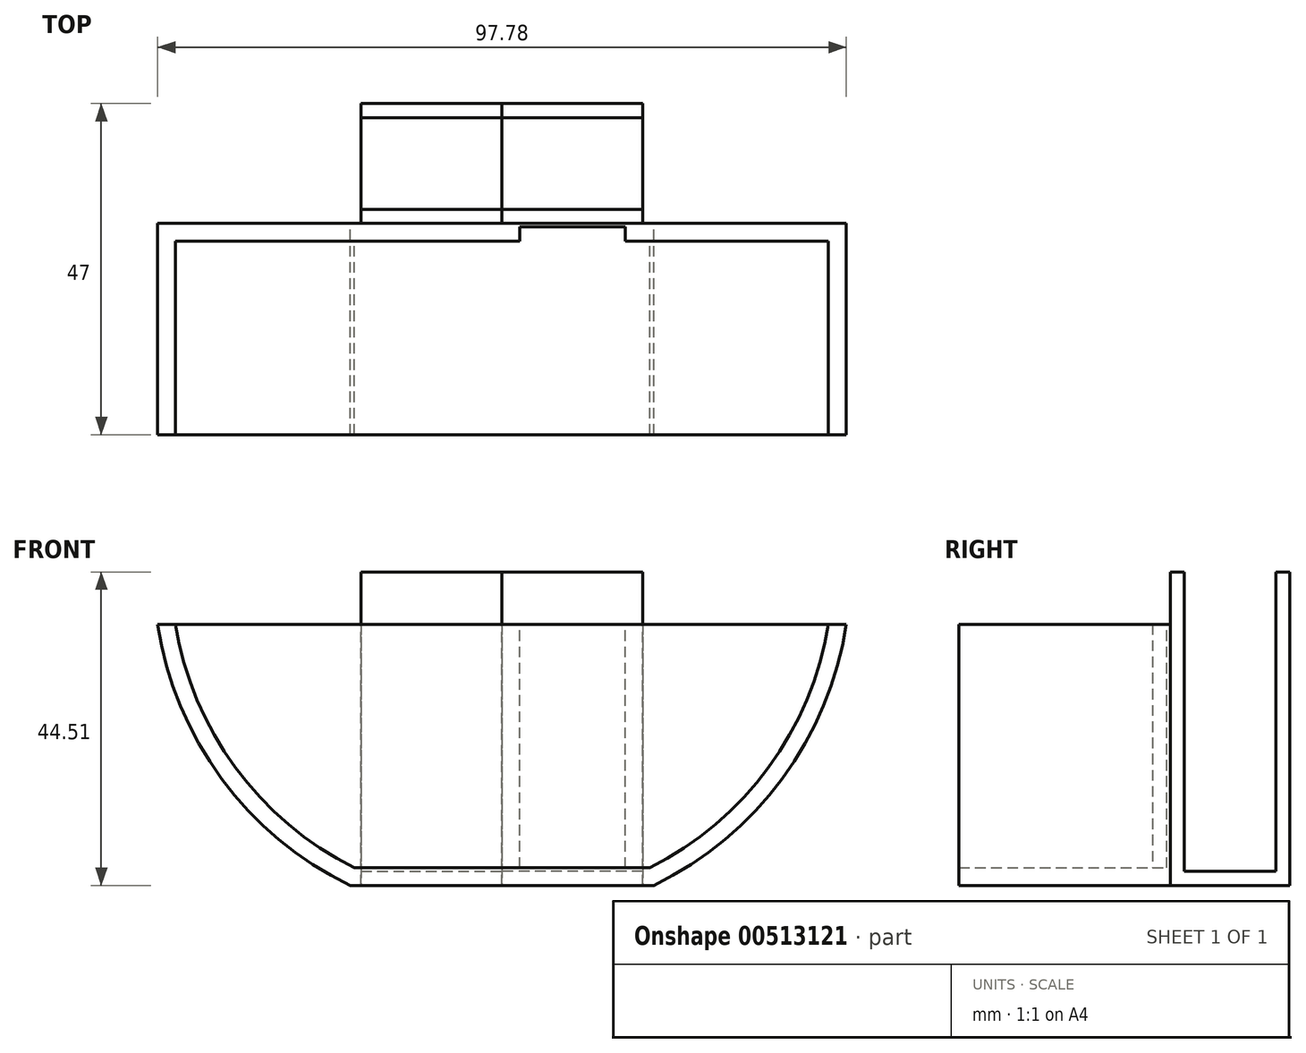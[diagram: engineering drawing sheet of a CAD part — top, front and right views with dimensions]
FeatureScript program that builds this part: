
annotation { "Feature Type Name" : "Feature", "Feature Type Description" : "" }
export const myFeature = defineFeature(function(context is Context, id is Id, definition is map)
    precondition{}
    {
        {
            var Q0;
            Q0=qCreatedBy(makeId("Front.planeOp"),FACE);
            var sketch = newSketch(context, id + "F0", { "sketchPlane" : qUnion([Q0])});
            skCircle(sketch, "E0", {"center": v(0, 0) * mm, "radius": 49.45 * mm});
            skLineSegment(sketch, "E1", {"start": v(-48.9, -7.42) * mm, "end": v(48.9, -7.42) * mm});
            skLineSegment(sketch, "E2", {"start": v(-21.56, -44.5) * mm, "end": v(21.56, -44.5) * mm});
            skSolve(sketch);
        }
        {
            var Q0;
            Q0=qCreatedBy(makeId("Right.planeOp"),FACE);
            var sketch = newSketch(context, id + "F1", { "sketchPlane" : qUnion([Q0])});
            skLineSegment(sketch, "E3", {"start": v(0, -44.5) * mm, "end": v(17, -44.5) * mm});
            skLineSegment(sketch, "E4", {"start": v(17, -44.5) * mm, "end": v(17, 0) * mm});
            skLineSegment(sketch, "E5", {"start": v(17, 0) * mm, "end": v(15, 0) * mm});
            skLineSegment(sketch, "E6", {"start": v(15, 0) * mm, "end": v(15, -42.5) * mm});
            skLineSegment(sketch, "E7", {"start": v(15, -42.5) * mm, "end": v(2, -42.5) * mm});
            skLineSegment(sketch, "E8", {"start": v(2, -42.5) * mm, "end": v(2, 0) * mm});
            skLineSegment(sketch, "E9", {"start": v(2, 0) * mm, "end": v(0, 0) * mm});
            skLineSegment(sketch, "E10", {"start": v(0, 0) * mm, "end": v(0, -44.5) * mm});
            skSolve(sketch);
        }
        {
            var Q0;
            Q0 = qSketchRegion(id + "F1", true);
            extrude(context, id + "F2", {"entities" : qUnion([Q0]), "depth" : 20 * mm});
        }
        {
            var Q0;
            {var subQ0=sQuery(id+"F0.wireOp",EDGE,"E1");Q0=makeQuery(id+"F0.imprint","IMPRINT",FACE,{"disambiguationData":[TD([[makeQuery(id+"F0.imprint","IMPRINT",EDGE,{"derivedFrom":subQ0}),-1.0]])]});}
            extrude(context, id + "F3", {"entities" : qUnion([Q0]), "operationType" : NewBodyOperationType.ADD, "depth" : 30 * mm});
        }
        {
            var Q0;
            Q0=makeQuery(id+"F2.opExtrude","SWEPT_BODY",BODY,{"disambiguationData":[OSD([sQuery(id+"F1.wireOp",EDGE,"E3"),sQuery(id+"F1.wireOp",EDGE,"E4"),sQuery(id+"F1.wireOp",EDGE,"E5"),sQuery(id+"F1.wireOp",EDGE,"E6"),sQuery(id+"F1.wireOp",EDGE,"E7"),sQuery(id+"F1.wireOp",EDGE,"E8"),sQuery(id+"F1.wireOp",EDGE,"E9"),sQuery(id+"F1.wireOp",EDGE,"E10")])]});
            var Q1;
            Q1=qCreatedBy(makeId("Right.planeOp"),FACE);
            mirror(context, id + "F4", {"entities" : qUnion([Q0]), "mirrorPlane" : qUnion([Q1])});
        }
        {
            var Q0;
            Q0=makeQuery(id+"F3.opExtrude","CAP_FACE",FACE,{"disambiguationData":[OSD([sQuery(id+"F0.wireOp",EDGE,"E0"),sQuery(id+"F0.wireOp",EDGE,"E1"),sQuery(id+"F0.wireOp",EDGE,"E2")])],"isStart":false});
            var Q1;
            Q1=makeQuery(id+"F3.opExtrude","SWEPT_FACE",FACE,{"disambiguationData":[OSD([sQuery(id+"F0.wireOp",EDGE,"E1")])]});
            var Q2;
            Q2=makeQuery(id+"F2.opExtrude","SWEPT_BODY",BODY,{"disambiguationData":[OSD([sQuery(id+"F1.wireOp",EDGE,"E3"),sQuery(id+"F1.wireOp",EDGE,"E4"),sQuery(id+"F1.wireOp",EDGE,"E5"),sQuery(id+"F1.wireOp",EDGE,"E6"),sQuery(id+"F1.wireOp",EDGE,"E7"),sQuery(id+"F1.wireOp",EDGE,"E8"),sQuery(id+"F1.wireOp",EDGE,"E9"),sQuery(id+"F1.wireOp",EDGE,"E10")])]});
            shell(context, id + "F5", {"entities" : qUnion([Q0, Q1]), "parts" : qUnion([Q2]), "thickness" : 2.5 * mm});
        }
    });
